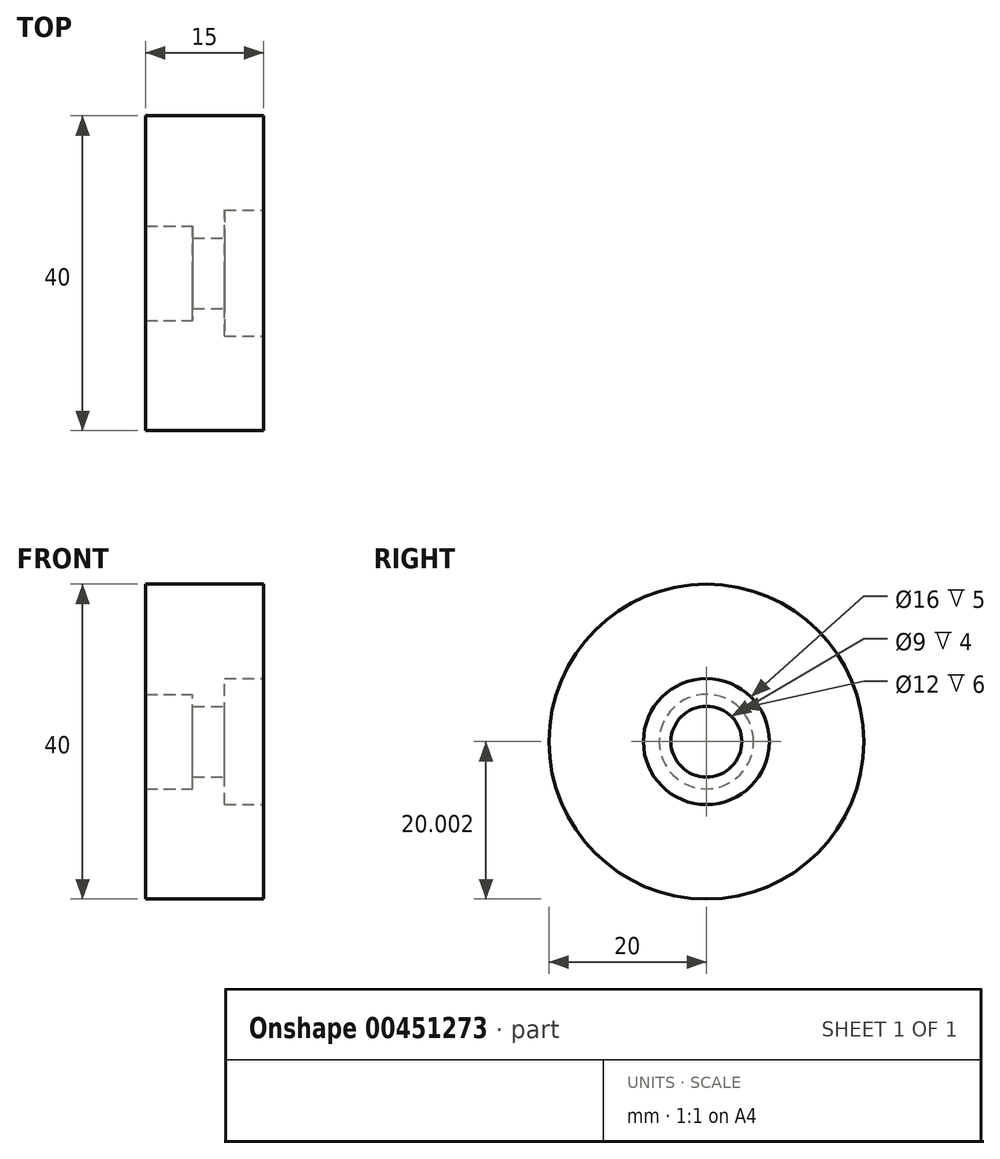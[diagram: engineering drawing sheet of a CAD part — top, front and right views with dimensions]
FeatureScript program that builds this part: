
annotation { "Feature Type Name" : "Feature", "Feature Type Description" : "" }
export const myFeature = defineFeature(function(context is Context, id is Id, definition is map)
    precondition{}
    {
        {
            var Q0;
            Q0=qCreatedBy(makeId("Front.planeOp"),FACE);
            var sketch = newSketch(context, id + "F0", { "sketchPlane" : qUnion([Q0])});
            skLineSegment(sketch, "E0", {"start": v(-43.36, -100.75) * mm, "end": v(-43.36, -84.75) * mm});
            skLineSegment(sketch, "E1", {"start": v(-43.36, -84.75) * mm, "end": v(-38.36, -84.75) * mm});
            skLineSegment(sketch, "E2", {"start": v(-43.36, -100.75) * mm, "end": v(-38.36, -100.75) * mm});
            skLineSegment(sketch, "E3", {"start": v(-38.36, -72.75) * mm, "end": v(-38.36, -112.75) * mm});
            skLineSegment(sketch, "E4", {"start": v(-53.36, -72.75) * mm, "end": v(-53.36, -112.75) * mm});
            skLineSegment(sketch, "E5", {"start": v(-47.36, -86.75) * mm, "end": v(-47.36, -98.75) * mm});
            skLineSegment(sketch, "E6", {"start": v(-43.36, -97.25) * mm, "end": v(-47.36, -97.25) * mm});
            skLineSegment(sketch, "E7", {"start": v(-43.36, -88.25) * mm, "end": v(-47.36, -88.25) * mm});
            skLineSegment(sketch, "E8", {"start": v(-35.84, -92.75) * mm, "end": v(-55.84, -92.75) * mm});
            skLineSegment(sketch, "E9", {"start": v(-47.36, -86.75) * mm, "end": v(-53.36, -86.75) * mm});
            skLineSegment(sketch, "E10", {"start": v(-47.36, -98.75) * mm, "end": v(-53.36, -98.75) * mm});
            skLineSegment(sketch, "E11", {"start": v(-38.36, -112.75) * mm, "end": v(-53.36, -112.75) * mm});
            skLineSegment(sketch, "E12", {"start": v(-38.36, -72.75) * mm, "end": v(-53.36, -72.75) * mm});
            skSolve(sketch);
        }
        {
            var Q0;
            {var subQ4=sQuery(id+"F0.wireOp",EDGE,"E2");Q0=makeQuery(id+"F0.imprint","IMPRINT",FACE,{"disambiguationData":[TD([[makeQuery(id+"F0.imprint","IMPRINT",EDGE,{"derivedFrom":subQ4}),-1.0]])]});}
            var Q1;
            Q1=sQuery(id+"F0.wireOp",EDGE,"E8");
            revolve(context, id + "F1", {"entities" : qUnion([Q0]), "axis" : qUnion([Q1]), "revolveType" : RevolveType.FULL});
        }
    });
